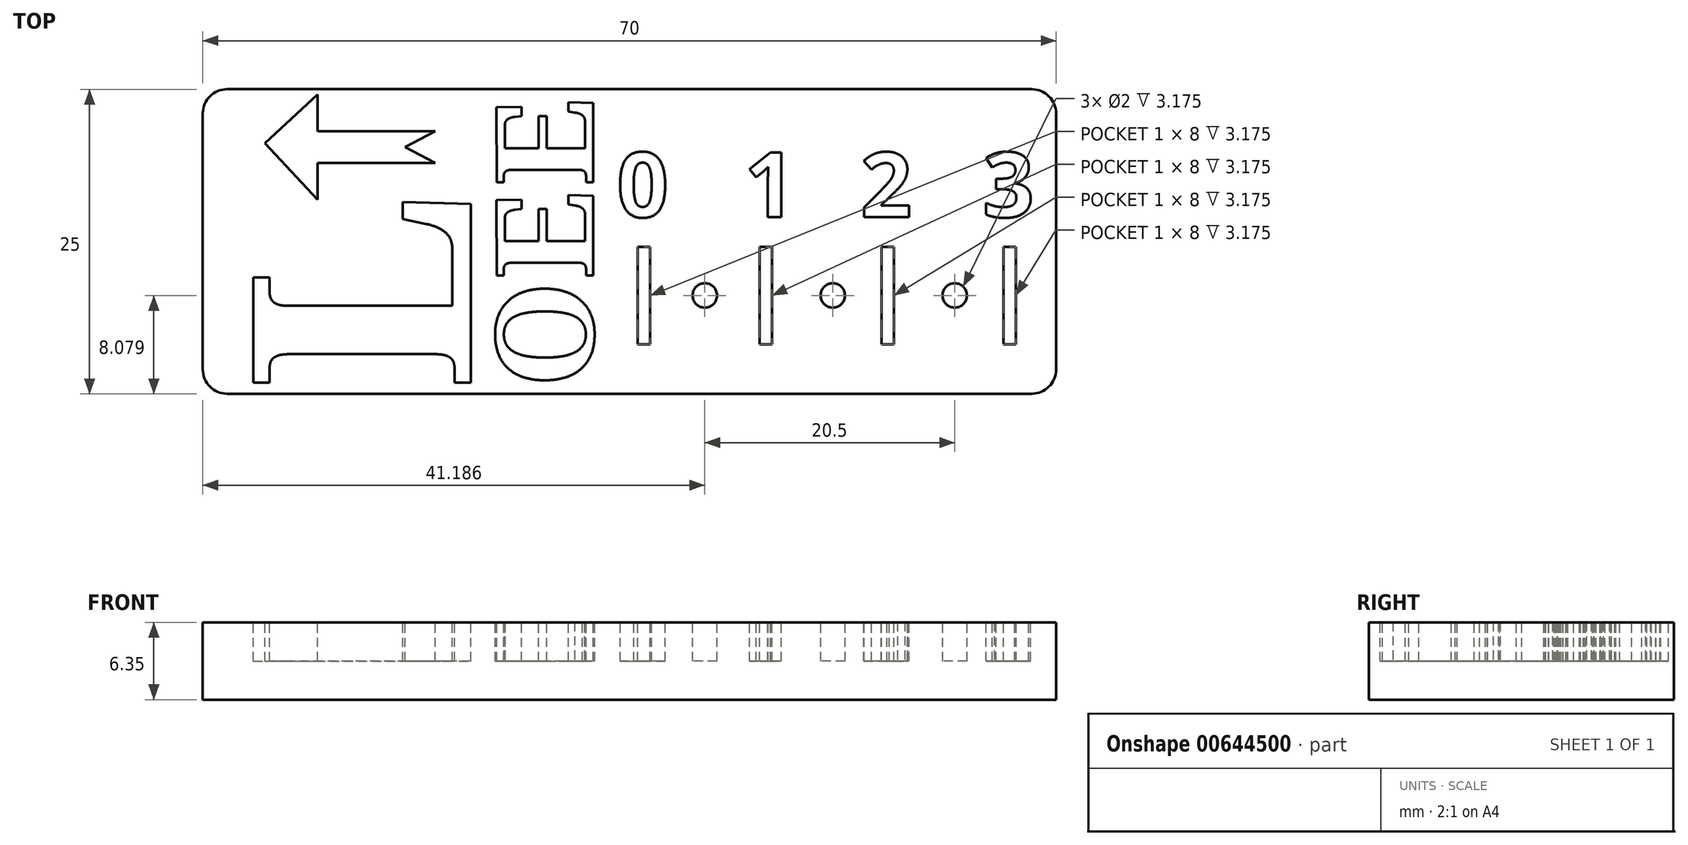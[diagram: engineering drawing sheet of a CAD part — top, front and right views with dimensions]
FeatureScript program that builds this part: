
annotation { "Feature Type Name" : "Feature", "Feature Type Description" : "" }
export const myFeature = defineFeature(function(context is Context, id is Id, definition is map)
    precondition{}
    {
        {
            var Q0;
            Q0=qCreatedBy(makeId("Top.planeOp"),FACE);
            var sketch = newSketch(context, id + "F0", { "sketchPlane" : qUnion([Q0])});
            skLineSegment(sketch, "E0.bottom", {"start": v(-55.27, 9.73) * mm, "end": v(10.73, 9.73) * mm});
            skLineSegment(sketch, "E0.top", {"start": v(-55.27, -15.27) * mm, "end": v(10.73, -15.27) * mm});
            skLineSegment(sketch, "E0.left", {"start": v(-57.27, 7.73) * mm, "end": v(-57.27, -13.27) * mm});
            skLineSegment(sketch, "E0.right", {"start": v(12.73, 7.73) * mm, "end": v(12.73, -13.27) * mm});
            skPoint(sketch, "E1.visualSharp", {"position": v(-57.27, 9.73) * mm});
            skArc(sketch, "E1.filletArc", {"start": v(-55.27, 9.73) * mm, "mid": v(-56.68, 9.15) * mm, "end": v(-57.27, 7.73) * mm});
            skPoint(sketch, "E2.visualSharp", {"position": v(12.73, 9.73) * mm});
            skArc(sketch, "E2.filletArc", {"start": v(12.73, 7.73) * mm, "mid": v(12.14, 9.15) * mm, "end": v(10.73, 9.73) * mm});
            skPoint(sketch, "E3.visualSharp", {"position": v(12.73, -15.27) * mm});
            skArc(sketch, "E3.filletArc", {"start": v(10.73, -15.27) * mm, "mid": v(12.14, -14.68) * mm, "end": v(12.73, -13.27) * mm});
            skPoint(sketch, "E4.visualSharp", {"position": v(-57.27, -15.27) * mm});
            skArc(sketch, "E4.filletArc", {"start": v(-57.27, -13.27) * mm, "mid": v(-56.68, -14.68) * mm, "end": v(-55.27, -15.27) * mm});
            skSolve(sketch);
        }
        {
            var Q0;
            Q0=qSketchRegion(id+"F0",true);
            extrude(context, id + "F1", {"entities" : qUnion([Q0]), "depth" : 6.35 * mm, "offsetDistance" : 25.4 * mm});
        }
        {
            var Q0;
            Q0=makeQuery(id+"F1.opExtrude","CAP_FACE",FACE,{"disambiguationData":[OSD([sQuery(id+"F0.wireOp",EDGE,"E0.bottom"),sQuery(id+"F0.wireOp",EDGE,"E0.top"),sQuery(id+"F0.wireOp",EDGE,"E0.left"),sQuery(id+"F0.wireOp",EDGE,"E0.right")])],"isStart":false});
            var sketch = newSketch(context, id + "F2", { "sketchPlane" : qUnion([Q0])});
            skText(sketch, "E5", { "text": "L", "fontName": "NotoSerif-Bold.ttf"});
            skText(sketch, "E6", { "text": "O\n", "fontName": "NotoSerif-Bold.ttf"});
            skText(sketch, "E7", { "text": "E", "fontName": "NotoSerif-Bold.ttf"});
            skLineSegment(sketch, "E8.bottom", {"start": v(-21.58, -3.2) * mm, "end": v(-20.58, -3.2) * mm});
            skLineSegment(sketch, "E8.top", {"start": v(-21.58, -11.2) * mm, "end": v(-20.58, -11.2) * mm});
            skLineSegment(sketch, "E8.left", {"start": v(-21.58, -3.2) * mm, "end": v(-21.58, -11.2) * mm});
            skLineSegment(sketch, "E8.right", {"start": v(-20.58, -3.2) * mm, "end": v(-20.58, -11.2) * mm});
            skLineSegment(sketch, "E9.bottom", {"start": v(-11.58, -3.2) * mm, "end": v(-10.58, -3.2) * mm});
            skLineSegment(sketch, "E9.top", {"start": v(-11.58, -11.2) * mm, "end": v(-10.58, -11.2) * mm});
            skLineSegment(sketch, "E9.left", {"start": v(-11.58, -3.2) * mm, "end": v(-11.58, -11.2) * mm});
            skLineSegment(sketch, "E9.right", {"start": v(-10.58, -3.2) * mm, "end": v(-10.58, -11.2) * mm});
            skLineSegment(sketch, "E10.bottom", {"start": v(-1.58, -3.2) * mm, "end": v(-0.58, -3.2) * mm});
            skLineSegment(sketch, "E10.top", {"start": v(-1.58, -11.2) * mm, "end": v(-0.58, -11.2) * mm});
            skLineSegment(sketch, "E10.left", {"start": v(-1.58, -3.2) * mm, "end": v(-1.58, -11.2) * mm});
            skLineSegment(sketch, "E10.right", {"start": v(-0.58, -3.2) * mm, "end": v(-0.58, -11.2) * mm});
            skLineSegment(sketch, "E11.bottom", {"start": v(8.42, -3.2) * mm, "end": v(9.42, -3.2) * mm});
            skLineSegment(sketch, "E11.top", {"start": v(8.42, -11.2) * mm, "end": v(9.42, -11.2) * mm});
            skLineSegment(sketch, "E11.left", {"start": v(8.42, -3.2) * mm, "end": v(8.42, -11.2) * mm});
            skLineSegment(sketch, "E11.right", {"start": v(9.42, -3.2) * mm, "end": v(9.42, -11.2) * mm});
            skPoint(sketch, "E12", {"position": v(-21.08, -3.2) * mm});
            skPoint(sketch, "E13", {"position": v(-11.08, -3.2) * mm});
            skPoint(sketch, "E14", {"position": v(-1.08, -3.2) * mm});
            skCircle(sketch, "E15", {"center": v(-16.08, -7.2) * mm, "radius": 1 * mm});
            skPoint(sketch, "E16", {"position": v(-20.58, -7.2) * mm});
            skCircle(sketch, "E17", {"center": v(-5.58, -7.2) * mm, "radius": 1 * mm});
            skCircle(sketch, "E18", {"center": v(4.42, -7.2) * mm, "radius": 1 * mm});
            skPoint(sketch, "E19", {"position": v(-10.58, -7.2) * mm});
            skPoint(sketch, "E20", {"position": v(-0.58, -7.2) * mm});
            skText(sketch, "E21", { "text": "0", "fontName": "OpenSans-Bold.ttf"});
            skText(sketch, "E22", { "text": "1", "fontName": "OpenSans-Bold.ttf"});
            skText(sketch, "E23", { "text": "2", "fontName": "OpenSans-Bold.ttf"});
            skText(sketch, "E24", { "text": "3", "fontName": "OpenSans-Bold.ttf"});
            skLineSegment(sketch, "E25", {"start": v(-38.2, 3.68) * mm, "end": v(-47.86, 3.68) * mm});
            skLineSegment(sketch, "E26", {"start": v(-47.86, 3.68) * mm, "end": v(-47.86, 0.68) * mm});
            skLineSegment(sketch, "E27", {"start": v(-47.86, 0.68) * mm, "end": v(-52.16, 5.3) * mm});
            skLineSegment(sketch, "E28", {"start": v(-52.16, 5.3) * mm, "end": v(-47.86, 9.3) * mm});
            skLineSegment(sketch, "E29", {"start": v(-47.86, 9.3) * mm, "end": v(-47.86, 6.3) * mm});
            skLineSegment(sketch, "E30", {"start": v(-47.86, 6.3) * mm, "end": v(-38.2, 6.3) * mm});
            skPoint(sketch, "E31", {"position": v(-40.68, 4.98) * mm});
            skLineSegment(sketch, "E32", {"start": v(-40.68, 4.98) * mm, "end": v(-38.2, 3.68) * mm});
            skLineSegment(sketch, "E33", {"start": v(-40.68, 4.98) * mm, "end": v(-38.2, 6.3) * mm});
            skText(sketch, "E34", { "text": "E", "fontName": "NotoSerif-Bold.ttf"});
            const initialGuessF2  = {"E5": [-0.03527, -0.01504, 0, 1, 0.018], "E6": [-0.02523, -0.01477, 0, 1, 0.008], "E7": [-0.02523, -0.00585, -0.00042, 1, 0.008], "E21": [-0.0233, -0.00076, 1, 0, 0.00534], "E22": [-0.01286, -0.00076, 1, 0, 0.00534], "E23": [-0.00332, -0.00076, 1, 0, 0.00534], "E24": [0.0067, -0.00076, 1, 0, 0.00534], "E34": [-0.02523, 0.00178, -0.00042, 1, 0.008]};
            skSetInitialGuess(sketch, initialGuessF2);
            skSolve(sketch);
        }
        {
            var Q0;
            Q0=qSketchRegion(id+"F2",true);
            extrude(context, id + "F3", {"entities" : qUnion([Q0]), "operationType" : NewBodyOperationType.REMOVE, "oppositeDirection" : true, "depth" : 3.17 * mm, "offsetDistance" : 25.4 * mm});
        }
    });
